# Revit family: Zumtobel EPURA
name_source: partatom
category: Lighting Fixtures
revit_build: Autodesk Revit 2016 (Build: 20150220_1215(x64)
units: mm (PartAtom-declared; Revit-internal decimal feet)

## family parameters
Always vertical = Yes
Cut with Voids When Loaded = No
Light Source = Yes
OmniClass Number = 23.80.70.11
OmniClass Title = Luminaries for Internal Lighting
Part Type = Normal
Room Calculation Point = No
Round Connector Dimension = Use Diameter
Shared = No
Work Plane-Based = No

## types (2) — shared parameters
Assembly Code = D5020210
Body = ZG_Metal_White
Color Filter = 16777215
Cover = ZG_Waveguide_Self_llumination_Opaque
Description = Free-standing luminaire
Dimming Lamp Color Temperature Shift = <None>
Emit Shape Visible in Rendering = No
Emit from Rectangle Length = 245 mm  [stored 0.803806 ft]
Emit from Rectangle Width = 549 mm  [stored 1.80118 ft]
Height = 1946 mm  [stored 6.38451 ft]
Lamp = LED
Manufacturer = Zumtobel Lighting
Photometric Web File = TLG_SP_0044135.IES
Tilt Angle = -90.00°
URL = http://www.zumtobel.com
Voltage = 230 V
Width = 325 mm  [stored 1.06627 ft]

## per-type parameters (varying)
| type | Apparent Load | Double Head | Length | Model | Single Head |
| EPURA Single Head | 118 VA | No | 629 mm | 42187081 | Yes |
| EPURA Double Head | 236 VA | Yes | 1369 mm  [stored 4.49147 ft] | 42186985 | No |

note: [stored X ft] marks values corroborated as IEEE doubles in the binary element streams (Revit-internal decimal feet)

## geometry (parser evidence)
native form markers: Blend x2, Sweep x5
no freeform markers — native parametric forms only
